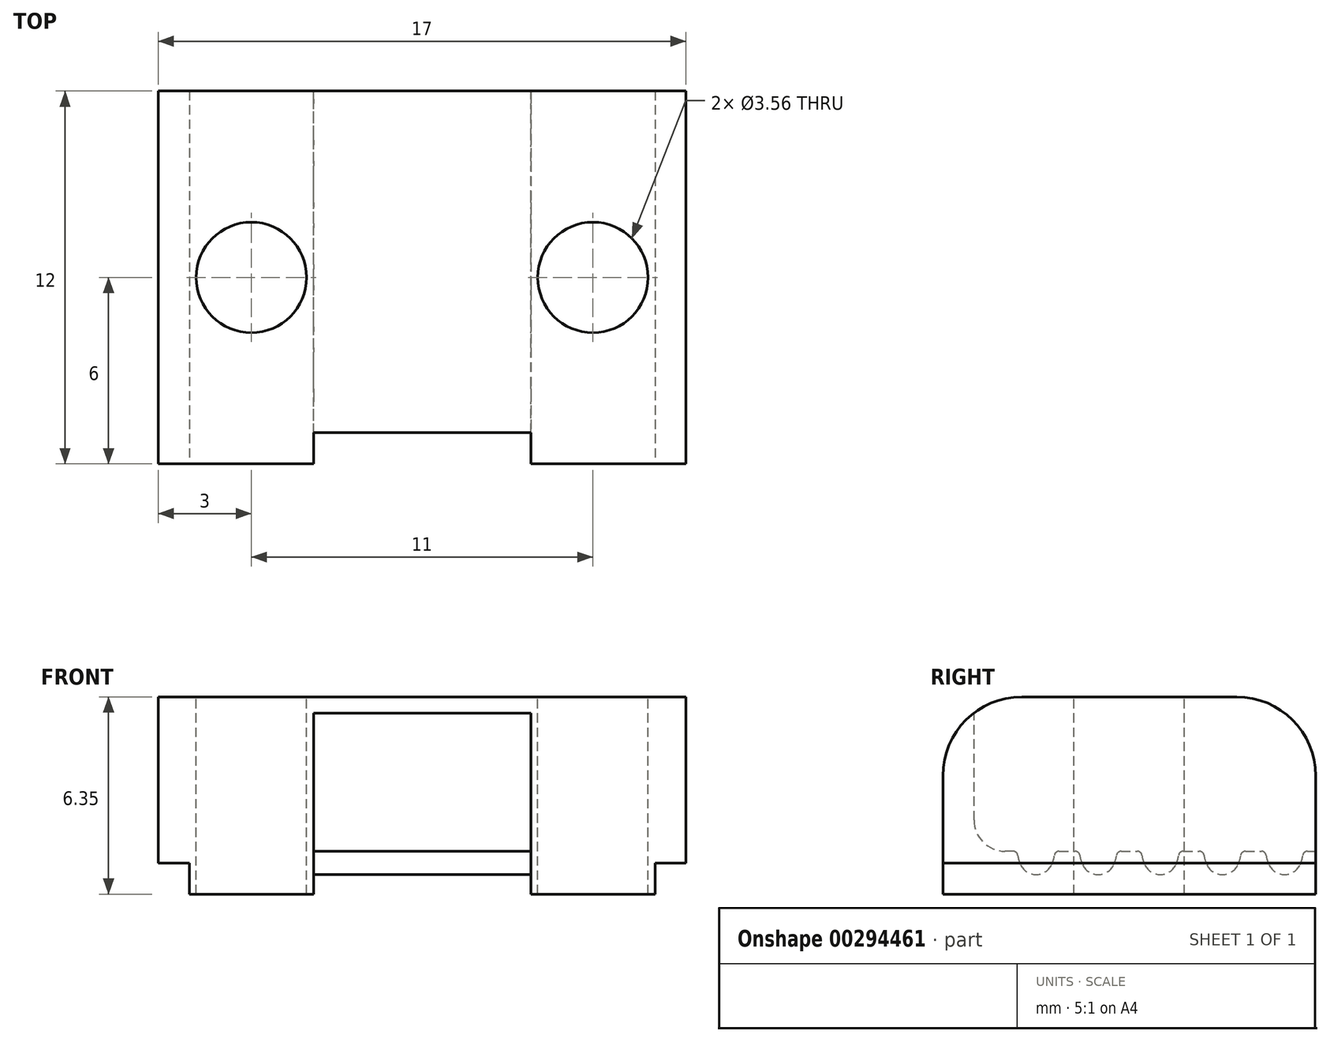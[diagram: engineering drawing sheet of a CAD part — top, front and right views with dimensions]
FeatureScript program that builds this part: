
annotation { "Feature Type Name" : "Feature", "Feature Type Description" : "" }
export const myFeature = defineFeature(function(context is Context, id is Id, definition is map)
    precondition{}
    {
        {
            var Q0;
            Q0=qCreatedBy(makeId("Right.planeOp"),FACE);
            var sketch = newSketch(context, id + "F0", { "sketchPlane" : qUnion([Q0])});
            skLineSegment(sketch, "E0.bottom", {"start": v(0, 0) * mm, "end": v(12, 0) * mm});
            skLineSegment(sketch, "E0.top", {"start": v(0, 6.35) * mm, "end": v(12, 6.35) * mm});
            skLineSegment(sketch, "E0.left", {"start": v(0, 0) * mm, "end": v(0, 6.35) * mm});
            skLineSegment(sketch, "E0.right", {"start": v(12, 0) * mm, "end": v(12, 6.35) * mm});
            skSolve(sketch);
        }
        {
            var Q0;
            Q0=makeQuery(id+"F0.imprint","IMPRINT",FACE,{"disambiguationData":[TD([[makeQuery(id+"F0.imprint","IMPRINT",EDGE,{"derivedFrom":sQuery(id+"F0.wireOp",EDGE,"E0.bottom")}),1.0]])]});
            extrude(context, id + "F1", {"entities" : qUnion([Q0]), "depth" : 4 * mm});
        }
        {
            var Q0;
            Q0=makeQuery(id+"F1.opExtrude","CAP_FACE",FACE,{"disambiguationData":[OSD([sQuery(id+"F0.wireOp",EDGE,"E0.bottom"),sQuery(id+"F0.wireOp",EDGE,"E0.top"),sQuery(id+"F0.wireOp",EDGE,"E0.left"),sQuery(id+"F0.wireOp",EDGE,"E0.right")])],"isStart":false});
            var sketch = newSketch(context, id + "F2", { "sketchPlane" : qUnion([Q0])});
            skLineSegment(sketch, "E1.bottom", {"start": v(12, 0) * mm, "end": v(0, 0) * mm});
            skLineSegment(sketch, "E1.top", {"start": v(12, 2.13) * mm, "end": v(0, 2.13) * mm, "construction": true});
            skLineSegment(sketch, "E1.left", {"start": v(12, 0) * mm, "end": v(12, 2.13) * mm, "construction": true});
            skLineSegment(sketch, "E1.right", {"start": v(0, 0) * mm, "end": v(0, 2.13) * mm});
            skLineSegment(sketch, "E2", {"start": v(12, 1.38) * mm, "end": v(10, 1.38) * mm, "construction": true});
            skLineSegment(sketch, "E3", {"start": v(11, 1.38) * mm, "end": v(11, 0.63) * mm, "construction": true});
            skLineSegment(sketch, "E4", {"start": v(12, 0.63) * mm, "end": v(10, 0.63) * mm, "construction": true});
            skArc(sketch, "E5", {"start": v(10.4, 1.25) * mm, "mid": v(10.44, 1.1) * mm, "end": v(10.5, 0.94) * mm});
            skArc(sketch, "E6.MirrorC", {"start": v(11.6, 1.25) * mm, "mid": v(11.56, 1.1) * mm, "end": v(11.5, 0.94) * mm});
            skArc(sketch, "E7", {"start": v(11.74, 1.38) * mm, "mid": v(11.64, 1.34) * mm, "end": v(11.6, 1.25) * mm});
            skArc(sketch, "E8.MirrorC", {"start": v(10.26, 1.38) * mm, "mid": v(10.36, 1.34) * mm, "end": v(10.4, 1.25) * mm});
            skArc(sketch, "E9.trimOffspring", {"start": v(10.5, 0.94) * mm, "mid": v(11, 0.63) * mm, "end": v(11.5, 0.94) * mm});
            skLineSegment(sketch, "E10", {"start": v(11.74, 1.38) * mm, "end": v(12, 1.38) * mm});
            skLineSegment(sketch, "E11", {"start": v(10.26, 1.38) * mm, "end": v(10, 1.38) * mm});
            skArc(sketch, "E12.1.0.0", {"start": v(8.4, 1.25) * mm, "mid": v(8.44, 1.1) * mm, "end": v(8.5, 0.94) * mm});
            skArc(sketch, "E12.1.0.1", {"start": v(8.5, 0.94) * mm, "mid": v(9, 0.63) * mm, "end": v(9.5, 0.94) * mm});
            skArc(sketch, "E12.1.0.2", {"start": v(9.6, 1.25) * mm, "mid": v(9.56, 1.1) * mm, "end": v(9.5, 0.94) * mm});
            skArc(sketch, "E12.1.0.3", {"start": v(9.74, 1.38) * mm, "mid": v(9.64, 1.34) * mm, "end": v(9.6, 1.25) * mm});
            skLineSegment(sketch, "E12.1.0.4", {"start": v(10, 0.63) * mm, "end": v(8, 0.63) * mm, "construction": true});
            skLineSegment(sketch, "E12.1.0.5", {"start": v(10, 1.38) * mm, "end": v(8, 1.38) * mm, "construction": true});
            skLineSegment(sketch, "E12.1.0.6", {"start": v(9, 1.38) * mm, "end": v(9, 0.63) * mm, "construction": true});
            skLineSegment(sketch, "E12.1.0.7", {"start": v(8.26, 1.38) * mm, "end": v(8, 1.38) * mm});
            skLineSegment(sketch, "E12.1.0.8", {"start": v(9.74, 1.38) * mm, "end": v(10, 1.38) * mm});
            skArc(sketch, "E12.1.0.9", {"start": v(8.26, 1.38) * mm, "mid": v(8.36, 1.34) * mm, "end": v(8.4, 1.25) * mm});
            skArc(sketch, "E12.2.0.0", {"start": v(6.4, 1.25) * mm, "mid": v(6.44, 1.1) * mm, "end": v(6.5, 0.94) * mm});
            skArc(sketch, "E12.2.0.1", {"start": v(6.5, 0.94) * mm, "mid": v(7, 0.63) * mm, "end": v(7.5, 0.94) * mm});
            skArc(sketch, "E12.2.0.2", {"start": v(7.6, 1.25) * mm, "mid": v(7.56, 1.1) * mm, "end": v(7.5, 0.94) * mm});
            skArc(sketch, "E12.2.0.3", {"start": v(7.74, 1.38) * mm, "mid": v(7.64, 1.34) * mm, "end": v(7.6, 1.25) * mm});
            skLineSegment(sketch, "E12.2.0.4", {"start": v(8, 0.63) * mm, "end": v(6, 0.63) * mm, "construction": true});
            skLineSegment(sketch, "E12.2.0.5", {"start": v(8, 1.38) * mm, "end": v(6, 1.38) * mm, "construction": true});
            skLineSegment(sketch, "E12.2.0.6", {"start": v(7, 1.38) * mm, "end": v(7, 0.63) * mm, "construction": true});
            skLineSegment(sketch, "E12.2.0.7", {"start": v(6.26, 1.38) * mm, "end": v(6, 1.38) * mm});
            skLineSegment(sketch, "E12.2.0.8", {"start": v(7.74, 1.38) * mm, "end": v(8, 1.38) * mm});
            skArc(sketch, "E12.2.0.9", {"start": v(6.26, 1.38) * mm, "mid": v(6.36, 1.34) * mm, "end": v(6.4, 1.25) * mm});
            skArc(sketch, "E12.3.0.0", {"start": v(4.4, 1.25) * mm, "mid": v(4.44, 1.1) * mm, "end": v(4.5, 0.94) * mm});
            skArc(sketch, "E12.3.0.1", {"start": v(4.5, 0.94) * mm, "mid": v(5, 0.63) * mm, "end": v(5.5, 0.94) * mm});
            skArc(sketch, "E12.3.0.2", {"start": v(5.6, 1.25) * mm, "mid": v(5.56, 1.1) * mm, "end": v(5.5, 0.94) * mm});
            skArc(sketch, "E12.3.0.3", {"start": v(5.74, 1.38) * mm, "mid": v(5.64, 1.34) * mm, "end": v(5.6, 1.25) * mm});
            skLineSegment(sketch, "E12.3.0.4", {"start": v(6, 0.63) * mm, "end": v(4, 0.63) * mm, "construction": true});
            skLineSegment(sketch, "E12.3.0.5", {"start": v(6, 1.38) * mm, "end": v(4, 1.38) * mm, "construction": true});
            skLineSegment(sketch, "E12.3.0.6", {"start": v(5, 1.38) * mm, "end": v(5, 0.63) * mm, "construction": true});
            skLineSegment(sketch, "E12.3.0.7", {"start": v(4.26, 1.38) * mm, "end": v(4, 1.38) * mm});
            skLineSegment(sketch, "E12.3.0.8", {"start": v(5.74, 1.38) * mm, "end": v(6, 1.38) * mm});
            skArc(sketch, "E12.3.0.9", {"start": v(4.26, 1.38) * mm, "mid": v(4.36, 1.34) * mm, "end": v(4.4, 1.25) * mm});
            skArc(sketch, "E12.4.0.0", {"start": v(2.4, 1.25) * mm, "mid": v(2.44, 1.1) * mm, "end": v(2.5, 0.94) * mm});
            skArc(sketch, "E12.4.0.1", {"start": v(2.5, 0.94) * mm, "mid": v(3, 0.63) * mm, "end": v(3.5, 0.94) * mm});
            skArc(sketch, "E12.4.0.2", {"start": v(3.6, 1.25) * mm, "mid": v(3.56, 1.1) * mm, "end": v(3.5, 0.94) * mm});
            skArc(sketch, "E12.4.0.3", {"start": v(3.74, 1.38) * mm, "mid": v(3.64, 1.34) * mm, "end": v(3.6, 1.25) * mm});
            skLineSegment(sketch, "E12.4.0.4", {"start": v(4, 0.63) * mm, "end": v(2, 0.63) * mm, "construction": true});
            skLineSegment(sketch, "E12.4.0.5", {"start": v(4, 1.38) * mm, "end": v(2, 1.38) * mm, "construction": true});
            skLineSegment(sketch, "E12.4.0.6", {"start": v(3, 1.38) * mm, "end": v(3, 0.63) * mm, "construction": true});
            skLineSegment(sketch, "E12.4.0.7", {"start": v(2.26, 1.38) * mm, "end": v(2, 1.38) * mm});
            skLineSegment(sketch, "E12.4.0.8", {"start": v(3.74, 1.38) * mm, "end": v(4, 1.38) * mm});
            skArc(sketch, "E12.4.0.9", {"start": v(2.26, 1.38) * mm, "mid": v(2.36, 1.34) * mm, "end": v(2.4, 1.25) * mm});
            skLineSegment(sketch, "E12.direction1", {"start": v(10, 0.63) * mm, "end": v(8, 0.63) * mm, "construction": true});
            skLineSegment(sketch, "E13", {"start": v(12, 0) * mm, "end": v(12, 1.38) * mm, "construction": true});
            skLineSegment(sketch, "E14", {"start": v(1, 2.38) * mm, "end": v(1, 6.35) * mm});
            skArc(sketch, "E15", {"start": v(1, 2.38) * mm, "mid": v(1.3, 1.67) * mm, "end": v(2, 1.38) * mm});
            skLineSegment(sketch, "E16", {"start": v(12, 1.38) * mm, "end": v(12, 6.35) * mm});
            skLineSegment(sketch, "E17", {"start": v(12, 6.35) * mm, "end": v(1, 6.35) * mm});
            skSolve(sketch);
        }
        {
            var Q0;
            Q0 = qSketchRegion(id + "F2", true);
            extrude(context, id + "F3", {"entities" : qUnion([Q0]), "operationType" : NewBodyOperationType.ADD, "depth" : 7 * mm});
        }
        {
            var Q0;
            Q0=makeQuery(id+"F3.opExtrude","CAP_FACE",FACE,{"disambiguationData":[OSD([sQuery(id+"F2.wireOp",EDGE,"E5"),sQuery(id+"F2.wireOp",EDGE,"E6.MirrorC"),sQuery(id+"F2.wireOp",EDGE,"E7"),sQuery(id+"F2.wireOp",EDGE,"E8.MirrorC"),sQuery(id+"F2.wireOp",EDGE,"E9.trimOffspring"),sQuery(id+"F2.wireOp",EDGE,"E10"),sQuery(id+"F2.wireOp",EDGE,"E11"),sQuery(id+"F2.wireOp",EDGE,"E12.1.0.0"),sQuery(id+"F2.wireOp",EDGE,"E12.1.0.1"),sQuery(id+"F2.wireOp",EDGE,"E12.1.0.2"),sQuery(id+"F2.wireOp",EDGE,"E12.1.0.3"),sQuery(id+"F2.wireOp",EDGE,"E12.1.0.7"),sQuery(id+"F2.wireOp",EDGE,"E12.1.0.8"),sQuery(id+"F2.wireOp",EDGE,"E12.1.0.9"),sQuery(id+"F2.wireOp",EDGE,"E12.2.0.0"),sQuery(id+"F2.wireOp",EDGE,"E12.2.0.1"),sQuery(id+"F2.wireOp",EDGE,"E12.2.0.2"),sQuery(id+"F2.wireOp",EDGE,"E12.2.0.3"),sQuery(id+"F2.wireOp",EDGE,"E12.2.0.7"),sQuery(id+"F2.wireOp",EDGE,"E12.2.0.8"),sQuery(id+"F2.wireOp",EDGE,"E12.2.0.9"),sQuery(id+"F2.wireOp",EDGE,"E12.3.0.0"),sQuery(id+"F2.wireOp",EDGE,"E12.3.0.1"),sQuery(id+"F2.wireOp",EDGE,"E12.3.0.2"),sQuery(id+"F2.wireOp",EDGE,"E12.3.0.3"),sQuery(id+"F2.wireOp",EDGE,"E12.3.0.7"),sQuery(id+"F2.wireOp",EDGE,"E12.3.0.8"),sQuery(id+"F2.wireOp",EDGE,"E12.3.0.9"),sQuery(id+"F2.wireOp",EDGE,"E12.4.0.0"),sQuery(id+"F2.wireOp",EDGE,"E12.4.0.1"),sQuery(id+"F2.wireOp",EDGE,"E12.4.0.2"),sQuery(id+"F2.wireOp",EDGE,"E12.4.0.3"),sQuery(id+"F2.wireOp",EDGE,"E12.4.0.7"),sQuery(id+"F2.wireOp",EDGE,"E12.4.0.8"),sQuery(id+"F2.wireOp",EDGE,"E12.4.0.9"),sQuery(id+"F2.wireOp",EDGE,"E14"),sQuery(id+"F2.wireOp",EDGE,"E15"),sQuery(id+"F2.wireOp",EDGE,"E16"),sQuery(id+"F2.wireOp",EDGE,"E17")])],"isStart":false});
            var sketch = newSketch(context, id + "F4", { "sketchPlane" : qUnion([Q0])});
            skLineSegment(sketch, "E18.bottom", {"start": v(12, 6.35) * mm, "end": v(0, 6.35) * mm});
            skLineSegment(sketch, "E18.top", {"start": v(12, 0) * mm, "end": v(0, 0) * mm});
            skLineSegment(sketch, "E18.left", {"start": v(12, 6.35) * mm, "end": v(12, 0) * mm});
            skLineSegment(sketch, "E18.right", {"start": v(0, 6.35) * mm, "end": v(0, 0) * mm});
            skSolve(sketch);
        }
        {
            var Q0;
            Q0 = qSketchRegion(id + "F4", true);
            extrude(context, id + "F5", {"entities" : qUnion([Q0]), "operationType" : NewBodyOperationType.ADD, "depth" : 4 * mm});
        }
        {
            var Q0;
            Q0=makeQuery(id+"F5.boolean.opBoolean","MERGE",FACE,{"derivedFrom":[makeQuery(id+"F3.boolean.opBoolean","MERGE",FACE,{"derivedFrom":[makeQuery(id+"F1.opExtrude","SWEPT_FACE",FACE,{"disambiguationData":[OSD([sQuery(id+"F0.wireOp",EDGE,"E0.top")])]}),makeQuery(id+"F3.opExtrude","SWEPT_FACE",FACE,{"disambiguationData":[OSD([sQuery(id+"F2.wireOp",EDGE,"E17")])]})]}),makeQuery(id+"F5.opExtrude","SWEPT_FACE",FACE,{"disambiguationData":[OSD([sQuery(id+"F4.wireOp",EDGE,"E18.bottom")])]})]});
            var sketch = newSketch(context, id + "F6", { "sketchPlane" : qUnion([Q0])});
            skCircle(sketch, "E19", {"center": v(2, 6) * mm, "radius": 1.78 * mm});
            skCircle(sketch, "E20", {"center": v(13, 6) * mm, "radius": 1.78 * mm});
            skLineSegment(sketch, "E21", {"start": v(13, 0) * mm, "end": v(13, 12) * mm, "construction": true});
            skLineSegment(sketch, "E22", {"start": v(2, 0) * mm, "end": v(2, 12) * mm, "construction": true});
            skSolve(sketch);
        }
        {
            var Q0;
            Q0 = qSketchRegion(id + "F6", true);
            extrude(context, id + "F7", {"entities" : qUnion([Q0]), "operationType" : NewBodyOperationType.REMOVE, "oppositeDirection" : true, "depth" : 25.4 * mm});
        }
        {
            var Q0;
            Q0=makeQuery(id+"F1.opExtrude","CAP_FACE",FACE,{"disambiguationData":[OSD([sQuery(id+"F0.wireOp",EDGE,"E0.bottom"),sQuery(id+"F0.wireOp",EDGE,"E0.top"),sQuery(id+"F0.wireOp",EDGE,"E0.left"),sQuery(id+"F0.wireOp",EDGE,"E0.right")])],"isStart":true});
            var sketch = newSketch(context, id + "F8", { "sketchPlane" : qUnion([Q0])});
            skLineSegment(sketch, "E23.bottom", {"start": v(-12, 6.35) * mm, "end": v(0, 6.35) * mm});
            skLineSegment(sketch, "E23.top", {"start": v(-12, 1) * mm, "end": v(0, 1) * mm});
            skLineSegment(sketch, "E23.left", {"start": v(-12, 6.35) * mm, "end": v(-12, 1) * mm});
            skLineSegment(sketch, "E23.right", {"start": v(0, 6.35) * mm, "end": v(0, 1) * mm});
            skSolve(sketch);
        }
        {
            var Q0;
            Q0 = qSketchRegion(id + "F8", true);
            extrude(context, id + "F9", {"entities" : qUnion([Q0]), "operationType" : NewBodyOperationType.ADD, "depth" : 1 * mm});
        }
        {
            var Q0;
            Q0=makeQuery(id+"F5.opExtrude","CAP_FACE",FACE,{"disambiguationData":[OSD([sQuery(id+"F4.wireOp",EDGE,"E18.bottom"),sQuery(id+"F4.wireOp",EDGE,"E18.top"),sQuery(id+"F4.wireOp",EDGE,"E18.left"),sQuery(id+"F4.wireOp",EDGE,"E18.right")])],"isStart":false});
            var sketch = newSketch(context, id + "F10", { "sketchPlane" : qUnion([Q0])});
            skLineSegment(sketch, "E24.bottom", {"start": v(12, 6.35) * mm, "end": v(0, 6.35) * mm});
            skLineSegment(sketch, "E24.top", {"start": v(12, 1) * mm, "end": v(0, 1) * mm});
            skLineSegment(sketch, "E24.left", {"start": v(12, 6.35) * mm, "end": v(12, 1) * mm});
            skLineSegment(sketch, "E24.right", {"start": v(0, 6.35) * mm, "end": v(0, 1) * mm});
            skSolve(sketch);
        }
        {
            var Q0;
            Q0 = qSketchRegion(id + "F10", true);
            extrude(context, id + "F11", {"entities" : qUnion([Q0]), "operationType" : NewBodyOperationType.ADD, "depth" : 1 * mm});
        }
        {
            var Q0;
            Q0=makeQuery(id+"F5.boolean.opBoolean","MERGE",EDGE,{"derivedFrom":[makeQuery(id+"F3.boolean.opBoolean","MERGE",EDGE,{"derivedFrom":[makeQuery(id+"F1.opExtrude","SWEPT_EDGE",EDGE,{"disambiguationData":[OSD([sQuery(id+"F0.wireOp",EDGE,"E0.top"),sQuery(id+"F0.wireOp",EDGE,"E0.right")])]}),makeQuery(id+"F3.opExtrude","SWEPT_EDGE",EDGE,{"disambiguationData":[OSD([sQuery(id+"F2.wireOp",EDGE,"E16"),sQuery(id+"F2.wireOp",EDGE,"E17")])]})]}),makeQuery(id+"F5.opExtrude","SWEPT_EDGE",EDGE,{"disambiguationData":[OSD([sQuery(id+"F4.wireOp",EDGE,"E18.bottom"),sQuery(id+"F4.wireOp",EDGE,"E18.left")])]})]});
            var Q1;
            Q1=makeQuery(id+"F1.opExtrude","SWEPT_EDGE",EDGE,{"disambiguationData":[OSD([sQuery(id+"F0.wireOp",EDGE,"E0.top"),sQuery(id+"F0.wireOp",EDGE,"E0.left")])]});
            var Q2;
            Q2=makeQuery(id+"F5.opExtrude","SWEPT_EDGE",EDGE,{"disambiguationData":[OSD([sQuery(id+"F4.wireOp",EDGE,"E18.bottom"),sQuery(id+"F4.wireOp",EDGE,"E18.right")])]});
            fillet(context, id + "F12", {"entities" : qUnion([Q0, Q1, Q2]), "radius" : 2.54 * mm, "tangentPropagation" : true, "allowEdgeOverflow" : false});
        }
    });
